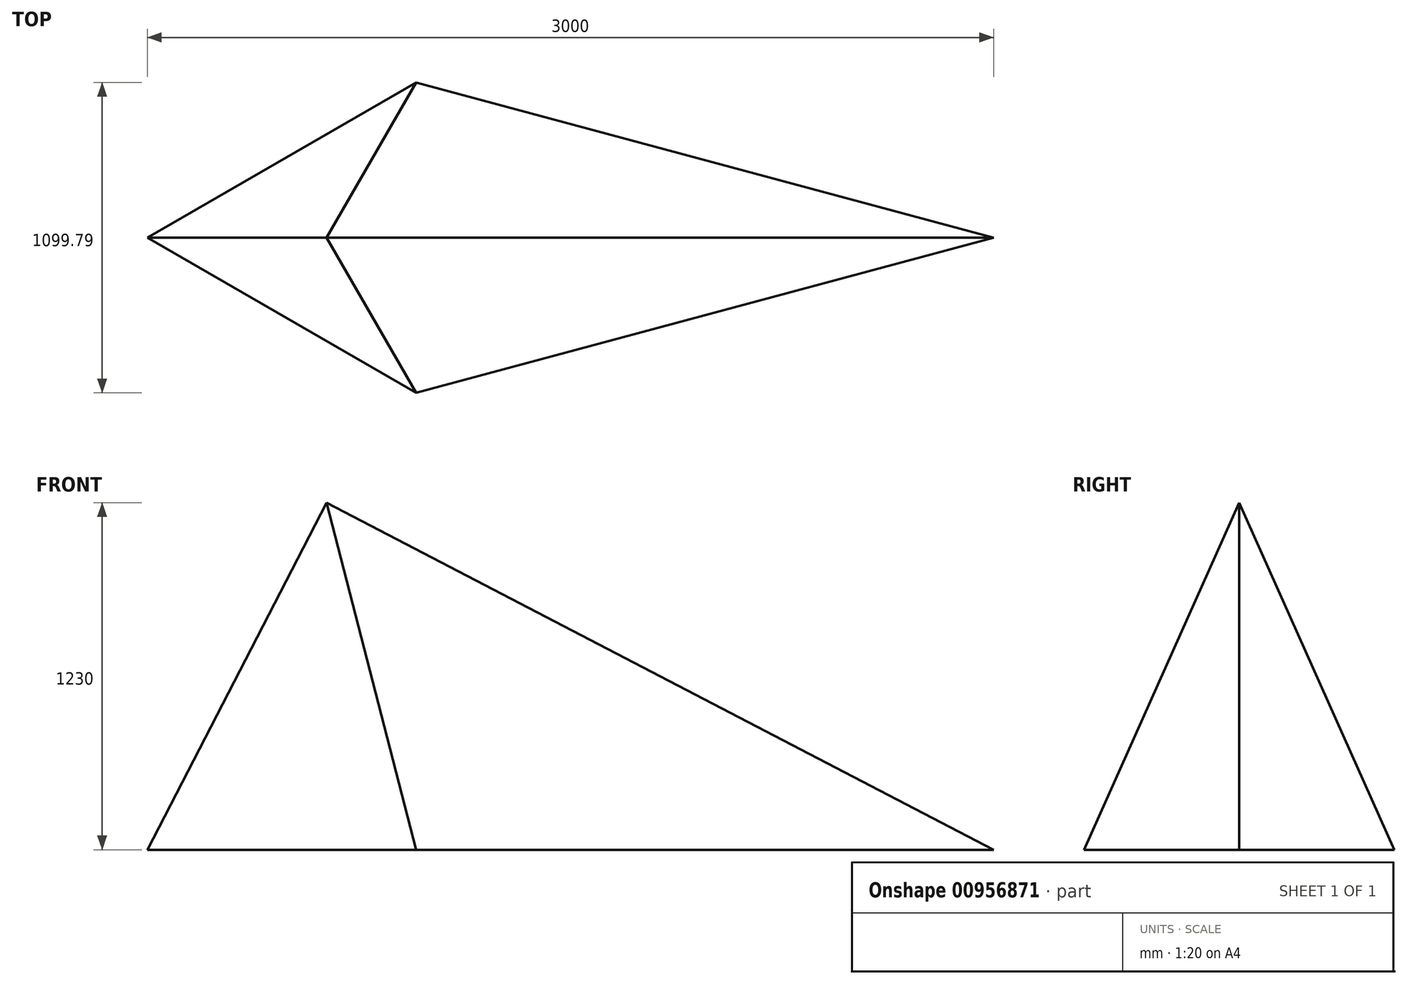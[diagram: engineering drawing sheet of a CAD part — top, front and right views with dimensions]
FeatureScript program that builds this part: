
annotation { "Feature Type Name" : "Feature", "Feature Type Description" : "" }
export const myFeature = defineFeature(function(context is Context, id is Id, definition is map)
    precondition{}
    {
        {
            var Q0;
            Q0=qCreatedBy(makeId("Top.planeOp"),FACE);
            var sketch = newSketch(context, id + "F0", { "sketchPlane" : qUnion([Q0])});
            skArc(sketch, "E0.cCircle", {"start": v(-8.08, 275) * mm, "mid": v(-8.08, -275) * mm, "end": v(468.24, 0) * mm, "construction": true});
            skLineSegment(sketch, "E0.1", {"start": v(468.24, -550) * mm, "end": v(-484.4, 0) * mm});
            skLineSegment(sketch, "E0.2", {"start": v(-484.4, 0) * mm, "end": v(468.24, 550) * mm});
            skPoint(sketch, "E0.0.midPoint", {"position": v(468.24, 0) * mm});
            skLineSegment(sketch, "E1.1", {"start": v(468.24, -550) * mm, "end": v(2515.6, 0) * mm});
            skLineSegment(sketch, "E1.2", {"start": v(2515.6, 0) * mm, "end": v(468.24, 550) * mm});
            skLineSegment(sketch, "E2.0", {"start": v(-484, 0) * mm, "end": v(468.26, 549.79) * mm});
            skLineSegment(sketch, "E2.1", {"start": v(468.26, -549.79) * mm, "end": v(-484, 0) * mm});
            skLineSegment(sketch, "E2.2", {"start": v(468.26, -549.79) * mm, "end": v(2514.84, 0) * mm});
            skLineSegment(sketch, "E2.3", {"start": v(2514.84, 0) * mm, "end": v(468.26, 549.79) * mm});
            skLineSegment(sketch, "E3", {"start": v(145.7, 0) * mm, "end": v(2145.7, 0) * mm});
            skLineSegment(sketch, "E4.left", {"start": v(2145.7, 99.16) * mm, "end": v(2145.6, -96.84) * mm});
            skLineSegment(sketch, "E5", {"start": v(150.7, 0) * mm, "end": v(-484, 0) * mm});
            skSolve(sketch);
        }
        {
            var Q0;
            Q0=qCreatedBy(makeId("Top.planeOp"),FACE);
            cPlane(context, id + "F1", {"entities" : qUnion([Q0]), "cplaneType" : CPlaneType.OFFSET, "offset" : 1230 * mm, "width" : 150 * mm, "height" : 150 * mm});
        }
        {
            var Q0;
            Q0=qCreatedBy(id+"F1.planeOp",FACE);
            var sketch = newSketch(context, id + "F2", { "sketchPlane" : qUnion([Q0])});
            skPoint(sketch, "E6.0", {"position": v(150.7, 0) * mm});
            skSolve(sketch);
        }
        {
            var Q0;
            Q0=sQuery(id+"F2.wireOp",VERTEX,"E6.0");
            var Q1;
            Q1=sQuery(id+"F0.wireOp",EDGE,"E1.1");
            loft(context, id + "F3", {"bodyType" : ToolBodyType.SURFACE, "wireProfilesArray" : [{ "wireProfileEntities" : qUnion([Q0]) }, { "wireProfileEntities" : qUnion([Q1]) }]});
        }
        {
            var Q0;
            Q0=sQuery(id+"F0.wireOp",EDGE,"E0.1");
            var Q1;
            Q1=sQuery(id+"F2.wireOp",VERTEX,"E6.0");
            loft(context, id + "F4", {"bodyType" : ToolBodyType.SURFACE, "wireProfilesArray" : [{ "wireProfileEntities" : qUnion([Q0]) }, { "wireProfileEntities" : qUnion([Q1]) }]});
        }
        {
            var Q0;
            Q0=sQuery(id+"F0.wireOp",EDGE,"E2.0");
            var Q1;
            Q1=sQuery(id+"F2.wireOp",VERTEX,"E6.0");
            loft(context, id + "F5", {"bodyType" : ToolBodyType.SURFACE, "wireProfilesArray" : [{ "wireProfileEntities" : qUnion([Q0]) }, { "wireProfileEntities" : qUnion([Q1]) }]});
        }
        {
            var Q0;
            Q0=sQuery(id+"F0.wireOp",EDGE,"E2.3");
            var Q1;
            Q1=sQuery(id+"F2.wireOp",VERTEX,"E6.0");
            loft(context, id + "F6", {"bodyType" : ToolBodyType.SURFACE, "wireProfilesArray" : [{ "wireProfileEntities" : qUnion([Q0]) }, { "wireProfileEntities" : qUnion([Q1]) }]});
        }
    });
